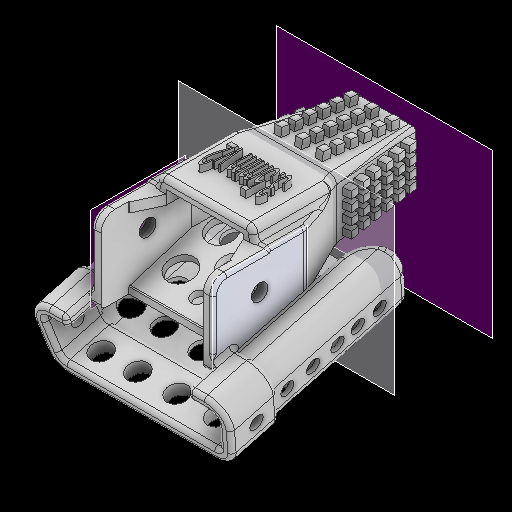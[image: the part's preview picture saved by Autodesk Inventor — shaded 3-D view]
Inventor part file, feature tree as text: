
AUTODESK INVENTOR PART (.ipt)
format: ipt  version: 2025 (Build 290162000, 162)  size: 3,375,616 bytes
history: native  units: mm
features: sketch x23, projected_geometry x20, delete_face x12, hole x9, fillet x8, extrude x8, thicken_offset x8, plane x7, other x3, loft x2, split x2, boolean_combine x2, thread x2, mirror x1, pattern_circular x1, emboss x1
ambient origin geometry x8: Origin, YZ Plane, XZ Plane, XY Plane, X Axis, Y Axis, Z Axis, Center Point
bodies: Solid1 (feature_tree), Solid8 (feature_tree), Solid2 (feature_tree), Solid4 (feature_tree), Solid5 (feature_tree), Solid6 (feature_tree), Solid7 (feature_tree)
feature tree (109):
  plane  "Work Plane6"
  loft  "Loft3"
  loft  "Loft4"
  fillet  "Fillet6"  [1 undecoded]
  sketch  "Sketch46"  dims[d284=0.0mm d287=0.45mm]
  extrude  "Grippers"  Depth=2.45mm
  mirror  "Mirror1"
  sketch  "Sketch47"  dims[d288=0.5mm d296=40.0mm d298=2.5mm d299=60.0mm d301=5.0mm d363=0.5mm d364=0.6mm d416=0.6mm d417=0.0mm d425=0.5mm]
  extrude  "FrontGrippers"  TaperAngle=0.0deg  [1 undecoded]
  sketch  "Sketch49"  dims[d426=60.0mm d428=5.0mm d429=10.0mm d431=10.0mm d433=20.0mm d435=1.5mm d436=20.0mm d438=1.5mm]
  extrude  "BackGrippers"  Depth=1.0mm TaperAngle=0.0deg
  plane  "Work Plane13"
  plane  "Work Plane14"
  extrude  "Extrusion16"  Depth=1.0mm TaperAngle=0.0deg
  extrude  "Extrusion19"  Depth=4.75mm
  extrude  "Extrusion21"  Depth=10.5mm
  extrude  "Extrusion22"  Depth=11.5mm
  plane  "Work Plane28"
  plane  "Work Plane29"
  split  "Split1"
  split  "Split2"
  extrude  "Extrusion34"  Depth=0.45mm
  boolean_combine  "Combine1"
  pattern_circular  "Circular Pattern1"  Count=4  [1 undecoded]
  delete_face  "Delete Face1"
  boolean_combine  "Combine2"
  thicken_offset  "Thicken1"
  thicken_offset  "Thicken2"
  thicken_offset  "Thicken3"
  fillet  "Fillet7"  Radius=0.5mm
  fillet  "Fillet8"  Radius=0.6mm
  fillet  "Fillet9"  Radius=0.6mm
  delete_face  "Delete Face2"
  delete_face  "Delete Face3"
  delete_face  "Delete Face4"
  delete_face  "Delete Face5"
  delete_face  "Delete Face6"
  delete_face  "Delete Face7"
  thicken_offset  "Thicken4"
  fillet  "Fillet10"  [1 undecoded]
  fillet  "Fillet11"  Radius=0.5mm
  hole  "Hole1"  [1 undecoded]
  hole  "Hole2"  [1 undecoded]
  hole  "Hole3"  [1 undecoded]
  hole  "Hole4"  [1 undecoded]
  hole  "Hole5"  [1 undecoded]
  hole  "Hole6"  [1 undecoded]
  thicken_offset  "Thicken5"
  thread  "Thread1"  [1 undecoded]
  thicken_offset  "Thicken6"
  thicken_offset  "Thicken7"
  thread  "Thread2"  [1 undecoded]
  thicken_offset  "Thicken8"
  hole  "Hole7"  [1 undecoded]
  delete_face  "Delete Face8"
  delete_face  "Delete Face9"
  delete_face  "Delete Face10"
  delete_face  "Delete Face11"
  delete_face  "Delete Face12"
  fillet  "Fillet12"  Radius=0.5mm
  fillet  "Fillet13"  Radius=2.0mm
  emboss  "Emboss1"
  hole  "Hole8"  [1 undecoded]
  hole  "Hole9"  [1 undecoded]
  plane  "Work Plane4"
  plane  "Work Plane5"
  sketch  "Sketch5"  dims[d30=0.0mm d31=90.0deg d32=0.0mm d33=90.0deg]
  other  "Edges3"
  sketch  "Sketch7"  dims[d126=1.0mm d127=0.0mm d135=15.0mm d136=0.0mm]
  other  "Edges4"
  sketch  "Sketch22"  dims[d140=1.0mm d141=0.0mm d142=15.0mm d143=0.0mm]
  projected_geometry  "Projected Loop8"
  sketch  "Sketch25"  dims[d156=9.5mm d157=4.75mm]
  sketch  "Sketch27"  dims[d158=10.5mm d159=5.25mm]
  sketch  "Sketch28"  dims[d160=12.5mm d162=11.5mm]
  sketch  "Sketch Rectangular Pattern1"  dims[d20=-7.1mm d22=4.5mm]
  sketch  "Sketch Rectangular Pattern2"  dims[d23=3.5mm d24=0.0mm d25=90.0deg d26=0.0mm d27=90.0deg]
  sketch  "Sketch Rectangular Pattern3"  dims[d28=2.85mm d29=2.45mm]
  projected_geometry  "Projected Loop36"
  projected_geometry  "Projected Loop37"
  projected_geometry  "Projected Loop38"
  projected_geometry  "Projected Loop39"
  projected_geometry  "Projected Loop40"
  projected_geometry  "Projected Loop41"
  projected_geometry  "Projected Loop42"
  projected_geometry  "Projected Loop43"
  projected_geometry  "Projected Loop44"
  projected_geometry  "Projected Loop45"
  projected_geometry  "Projected Loop46"
  projected_geometry  "Projected Loop47"
  projected_geometry  "Projected Loop48"
  projected_geometry  "Projected Loop49"
  projected_geometry  "Projected Loop50"
  projected_geometry  "Projected Loop51"
  projected_geometry  "Projected Loop52"
  projected_geometry  "Projected Loop53"
  sketch  "Sketch50"  dims[d441=0.6mm d442=0.0mm]
  projected_geometry  "Projected Loop54"
  other  "Pattern of Solid6:1"
  sketch  "Sketch51"  dims[d444=6.25mm d445=5.75mm]
  sketch  "Sketch52"  dims[d447=0.25mm d448=0.0mm]
  sketch  "Sketch53"  dims[d449=0.0mm d450=7.5mm d451=0.0mm]
  sketch  "Sketch54"  dims[d452=20.0mm d453=15.0deg d456=10.0mm d457=10.0mm d458=0.5mm]
  sketch  "Sketch55"  dims[d459=0.5mm d460=0.5mm d461=0.5mm d462=2.0mm]
  sketch  "Sketch56"  dims[d463=2.0mm d464=0.5mm]
  sketch  "Sketch57"  dims[d465=2.0mm d466=2.0mm]
  sketch  "Sketch58"  dims[d467=0.3mm]
  sketch  "Sketch59"  dims[d468=0.3mm]
  sketch  "Sketch60"  dims[d469=1.0mm d470=6.0mm d471=3.023mm d472=2.0mm d473=14.3117mm d474=1.0mm d475=0.0mm d476=1.0mm d477=6.0mm d478=4.0mm d479=2.0mm d480=90.0deg d481=1.0mm d482=0.0mm d483=1.0mm d484=6.0mm d485=4.0mm d486=2.0mm d487=90.0deg d488=1.0mm d489=0.0mm d490=1.0mm d491=6.0mm d492=4.0mm d493=2.0mm d494=90.0deg d495=1.0mm d496=0.0mm d497=1.5mm d498=6.0mm d499=4.0mm d500=2.0mm d501=90.0deg d502=1.0mm d503=0.0mm d504=1.5mm d505=6.0mm d506=4.0mm d507=2.0mm d508=90.0deg d509=1.0mm d510=0.0mm d511=0.2mm d512=0.2mm d513=0.7mm d514=0.0mm d515=0.2mm d516=0.2mm d517=0.2mm d518=0.2mm d519=0.7mm d520=0.0mm d521=0.2mm d522=0.2mm d523=2.7mm d524=6.0mm d525=3.023mm d526=2.0mm d527=14.3117mm d528=1.0mm d529=0.0mm d530=0.1mm d531=0.1mm d532=0.5mm d533=0.0mm d534=2.0mm d535=6.0mm d536=3.023mm d537=2.0mm d538=14.3117mm d539=1.0mm d540=0.0mm d541=1.0mm d542=6.0mm d543=4.0mm d544=2.0mm d545=90.0deg d546=1.0mm d547=0.0mm d39=0.5mm d40=0.872665mm d41=0.5mm d42=0.872665mm d193=0.5mm d194=0.872665mm d195=0.5mm d196=0.872665mm]
note: 15 required parameter values undecoded (feature->parameter linkage not recoverable at this tier; creation-order binding heuristic only, values carry confidence <= 0.55)
